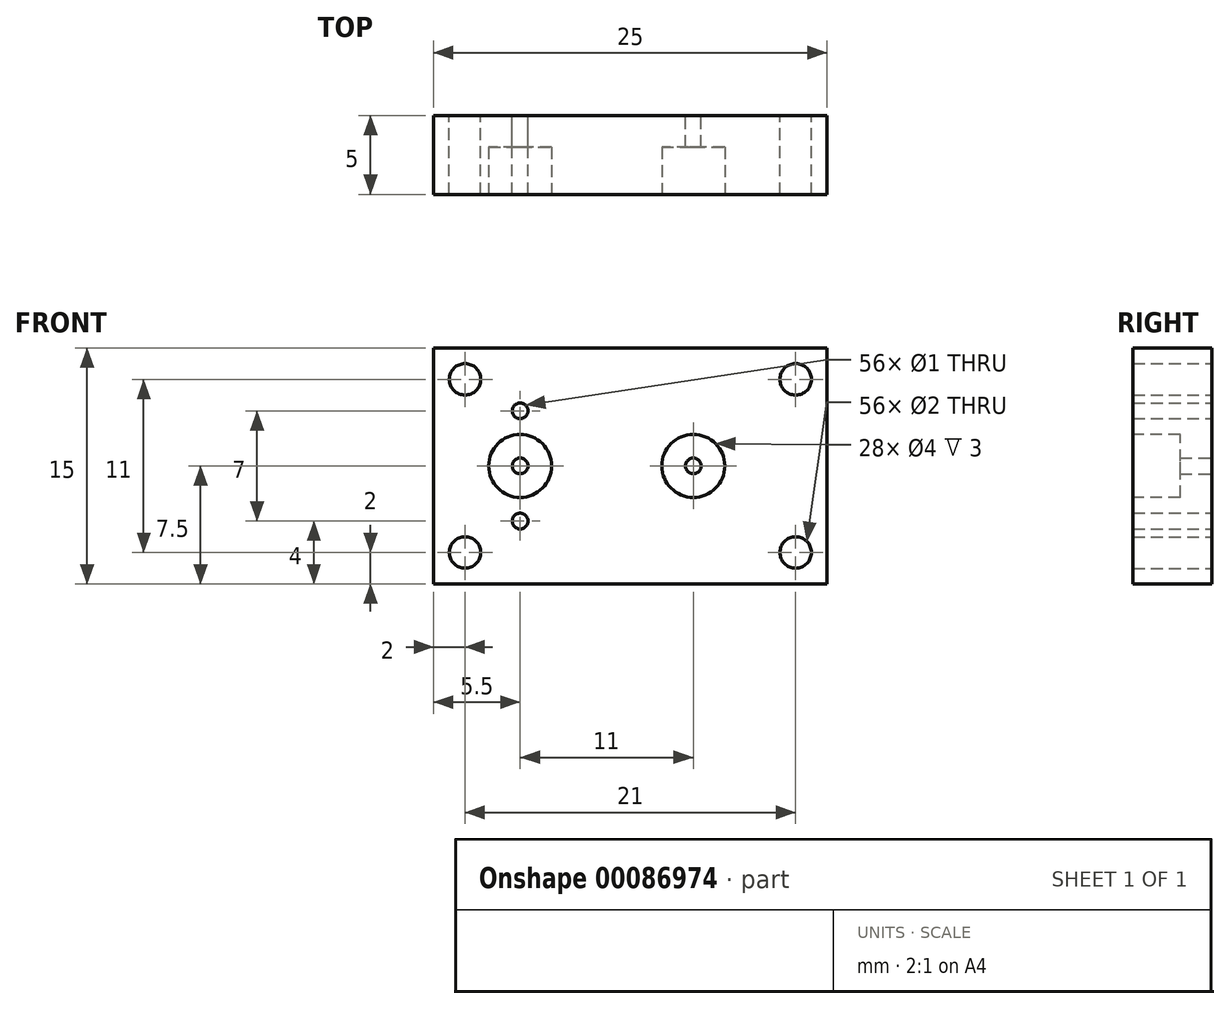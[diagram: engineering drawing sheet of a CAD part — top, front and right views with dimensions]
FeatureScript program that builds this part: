
annotation { "Feature Type Name" : "Feature", "Feature Type Description" : "" }
export const myFeature = defineFeature(function(context is Context, id is Id, definition is map)
    precondition{}
    {
        {
            var Q0;
            Q0=qCreatedBy(makeId("Front.planeOp"),FACE);
            var sketch = newSketch(context, id + "F0", { "sketchPlane" : qUnion([Q0])});
            skLineSegment(sketch, "E0.bottom", {"start": v(12.5, -7.5) * mm, "end": v(-12.5, -7.5) * mm});
            skLineSegment(sketch, "E0.top", {"start": v(12.5, 7.5) * mm, "end": v(-12.5, 7.5) * mm});
            skLineSegment(sketch, "E0.left", {"start": v(12.5, -7.5) * mm, "end": v(12.5, 7.5) * mm});
            skLineSegment(sketch, "E0.right", {"start": v(-12.5, -7.5) * mm, "end": v(-12.5, 7.5) * mm});
            skPoint(sketch, "E0.middle", {"position": v(0, 0) * mm});
            skCircle(sketch, "E1", {"center": v(-7, 0) * mm, "radius": 0.5 * mm});
            skCircle(sketch, "E2", {"center": v(4, 0) * mm, "radius": 0.5 * mm});
            skLineSegment(sketch, "E3", {"start": v(-7, 0) * mm, "end": v(4, 0) * mm});
            skLineSegment(sketch, "E4", {"start": v(-7, 3.5) * mm, "end": v(-7, -3.5) * mm, "construction": true});
            skCircle(sketch, "E5", {"center": v(-7, 3.5) * mm, "radius": 0.5 * mm});
            skCircle(sketch, "E6", {"center": v(-7, -3.5) * mm, "radius": 0.5 * mm});
            skCircle(sketch, "E7", {"center": v(-7, 0) * mm, "radius": 2.5 * mm, "construction": true});
            skCircle(sketch, "E8", {"center": v(4, 0) * mm, "radius": 6 * mm, "construction": true});
            skLineSegment(sketch, "E9.bottom", {"start": v(-10.5, 5.5) * mm, "end": v(10.5, 5.5) * mm, "construction": true});
            skLineSegment(sketch, "E9.top", {"start": v(-10.5, -5.5) * mm, "end": v(10.5, -5.5) * mm, "construction": true});
            skLineSegment(sketch, "E9.left", {"start": v(-10.5, 5.5) * mm, "end": v(-10.5, -5.5) * mm, "construction": true});
            skLineSegment(sketch, "E9.right", {"start": v(10.5, 5.5) * mm, "end": v(10.5, -5.5) * mm, "construction": true});
            skCircle(sketch, "E10", {"center": v(-10.5, 5.5) * mm, "radius": 1 * mm});
            skCircle(sketch, "E11", {"center": v(-10.5, -5.5) * mm, "radius": 1 * mm});
            skCircle(sketch, "E12", {"center": v(10.5, -5.5) * mm, "radius": 1 * mm});
            skCircle(sketch, "E13", {"center": v(10.5, 5.5) * mm, "radius": 1 * mm});
            skSolve(sketch);
        }
        {
            var Q0;
            Q0 = qSketchRegion(id + "F0", true);
            var Q1;
            Q1=makeQuery(id+"F0.imprint","IMPRINT",FACE,{"disambiguationData":[TD([[makeQuery(id+"F0.imprint","IMPRINT",EDGE,{"derivedFrom":sQuery(id+"F0.wireOp",EDGE,"E1")}),-1.0]])]});
            var Q2;
            Q2=makeQuery(id+"F0.imprint","IMPRINT",FACE,{"disambiguationData":[TD([[makeQuery(id+"F0.imprint","IMPRINT",EDGE,{"derivedFrom":sQuery(id+"F0.wireOp",EDGE,"E2")}),-1.0]])]});
            extrude(context, id + "F1", {"entities" : qUnion([Q0, Q1, Q2]), "depth" : 5 * mm});
        }
        {
            var Q0;
            Q0=makeQuery(id+"F1.opExtrude","CAP_FACE",FACE,{"disambiguationData":[OSD([sQuery(id+"F0.wireOp",EDGE,"E0.bottom"),sQuery(id+"F0.wireOp",EDGE,"E0.top"),sQuery(id+"F0.wireOp",EDGE,"E0.left"),sQuery(id+"F0.wireOp",EDGE,"E0.right"),sQuery(id+"F0.wireOp",EDGE,"E1"),sQuery(id+"F0.wireOp",EDGE,"E2"),sQuery(id+"F0.wireOp",EDGE,"E5"),sQuery(id+"F0.wireOp",EDGE,"E6"),sQuery(id+"F0.wireOp",EDGE,"E10"),sQuery(id+"F0.wireOp",EDGE,"E11"),sQuery(id+"F0.wireOp",EDGE,"E12"),sQuery(id+"F0.wireOp",EDGE,"E13")])],"isStart":false});
            var sketch = newSketch(context, id + "F2", { "sketchPlane" : qUnion([Q0])});
            skCircle(sketch, "E14", {"center": v(-7, 0) * mm, "radius": 2 * mm});
            skCircle(sketch, "E15", {"center": v(4, 0) * mm, "radius": 2 * mm});
            skSolve(sketch);
        }
        {
            var Q0;
            Q0=makeQuery(id+"F2.imprint","IMPRINT",FACE,{"disambiguationData":[TD([[makeQuery(id+"F2.imprint","IMPRINT",EDGE,{"derivedFrom":makeQuery(id+"F1.opExtrude","CAP_EDGE",EDGE,{"disambiguationData":[OSD([sQuery(id+"F0.wireOp",EDGE,"E1")])],"isStart":false})}),-1.0]])]});
            var Q1;
            Q1=makeQuery(id+"F2.imprint","IMPRINT",FACE,{"disambiguationData":[TD([[makeQuery(id+"F2.imprint","IMPRINT",EDGE,{"derivedFrom":sQuery(id+"F2.wireOp",EDGE,"E15")}),1.0]])]});
            extrude(context, id + "F3", {"entities" : qUnion([Q0, Q1]), "operationType" : NewBodyOperationType.REMOVE, "oppositeDirection" : true, "depth" : 3 * mm});
        }
    });
